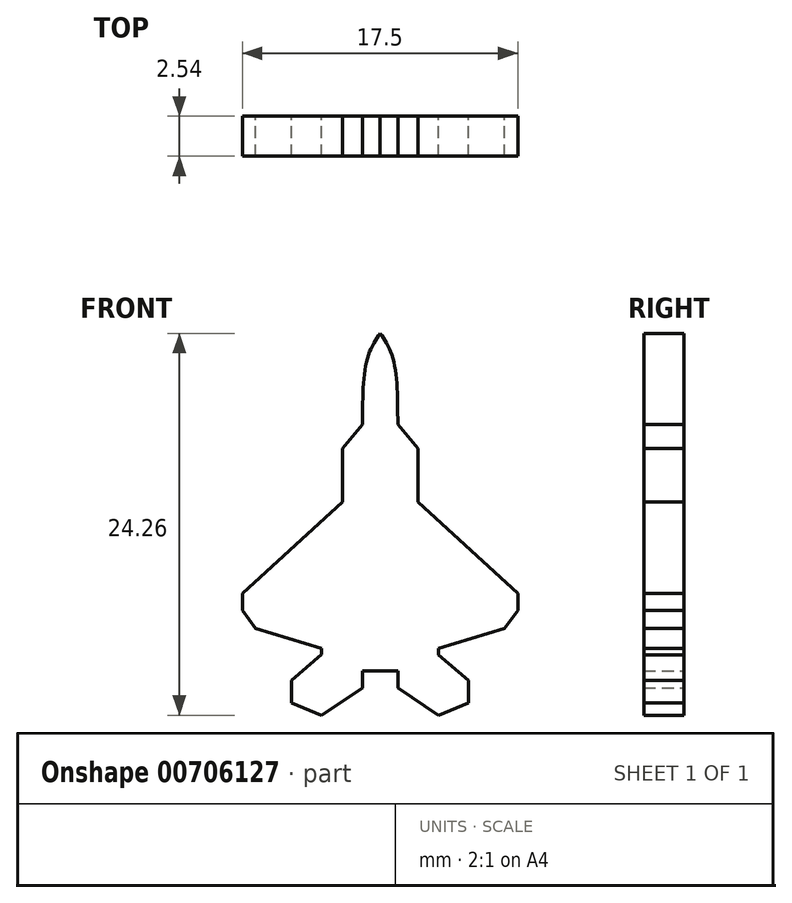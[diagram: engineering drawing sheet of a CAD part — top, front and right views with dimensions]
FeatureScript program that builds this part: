
annotation { "Feature Type Name" : "Feature", "Feature Type Description" : "" }
export const myFeature = defineFeature(function(context is Context, id is Id, definition is map)
    precondition{}
    {
        {
            var Q0;
            Q0=qCreatedBy(makeId("Front.planeOp"),FACE);
            var sketch = newSketch(context, id + "F0", { "sketchPlane" : qUnion([Q0])});
            skLineSegment(sketch, "E0.bottom", {"start": v(12.7, 12.7) * mm, "end": v(-12.7, 12.7) * mm});
            skLineSegment(sketch, "E0.top", {"start": v(12.7, -12.7) * mm, "end": v(-12.7, -12.7) * mm});
            skLineSegment(sketch, "E0.left", {"start": v(12.7, 12.7) * mm, "end": v(12.7, -12.7) * mm});
            skLineSegment(sketch, "E0.right", {"start": v(-12.7, 12.7) * mm, "end": v(-12.7, -12.7) * mm});
            skPoint(sketch, "E0.middle", {"position": v(0, 0) * mm});
            skSolve(sketch);
        }
        {
            var Q0;
            Q0 = qSketchRegion(id + "F0", true);
            extrude(context, id + "F1", {"entities" : qUnion([Q0]), "depth" : 6.35 * mm, "offsetDistance" : 25.4 * mm});
        }
        {
            var Q0;
            Q0=makeQuery(id+"F1.opExtrude","CAP_FACE",FACE,{"disambiguationData":[OSD([sQuery(id+"F0.wireOp",EDGE,"E0.bottom"),sQuery(id+"F0.wireOp",EDGE,"E0.top"),sQuery(id+"F0.wireOp",EDGE,"E0.left"),sQuery(id+"F0.wireOp",EDGE,"E0.right")])],"isStart":false});
            var sketch = newSketch(context, id + "F2", { "sketchPlane" : qUnion([Q0])});
            skLineSegment(sketch, "E1", {"start": v(-1.12, 6.26) * mm, "end": v(-2.4, 4.72) * mm});
            skLineSegment(sketch, "E2", {"start": v(-2.4, 1.33) * mm, "end": v(-8.75, -4.5) * mm});
            skLineSegment(sketch, "E3", {"start": v(-8.75, -4.5) * mm, "end": v(-8.75, -5.56) * mm});
            skLineSegment(sketch, "E4", {"start": v(-8.75, -5.56) * mm, "end": v(-7.9, -6.72) * mm});
            skLineSegment(sketch, "E5", {"start": v(-7.9, -6.72) * mm, "end": v(-3.72, -8) * mm});
            skLineSegment(sketch, "E6", {"start": v(-3.72, -8) * mm, "end": v(-5.62, -10) * mm});
            skLineSegment(sketch, "E7", {"start": v(-5.62, -10) * mm, "end": v(-5.62, -11.44) * mm});
            skLineSegment(sketch, "E8", {"start": v(-5.62, -11.44) * mm, "end": v(-3.72, -12.23) * mm});
            skLineSegment(sketch, "E9", {"start": v(-3.72, -12.23) * mm, "end": v(-1.12, -10.48) * mm});
            skLineSegment(sketch, "E10", {"start": v(-1.12, -10.48) * mm, "end": v(-1.12, -9.42) * mm});
            skLineSegment(sketch, "E11.MirrorCS", {"start": v(8.75, -4.5) * mm, "end": v(8.75, -5.56) * mm});
            skLineSegment(sketch, "E12.MirrorCS", {"start": v(8.75, -5.56) * mm, "end": v(7.9, -6.72) * mm});
            skLineSegment(sketch, "E13.MirrorCS", {"start": v(1.12, -10.48) * mm, "end": v(1.12, -9.42) * mm});
            skLineSegment(sketch, "E14.MirrorCS", {"start": v(3.72, -12.23) * mm, "end": v(1.12, -10.48) * mm});
            skLineSegment(sketch, "E15.MirrorCS", {"start": v(5.62, -11.44) * mm, "end": v(3.72, -12.23) * mm});
            skLineSegment(sketch, "E16.MirrorCS", {"start": v(1.12, 6.26) * mm, "end": v(2.4, 4.72) * mm});
            skLineSegment(sketch, "E17.MirrorCS", {"start": v(5.62, -10) * mm, "end": v(5.62, -11.44) * mm});
            skLineSegment(sketch, "E18.MirrorCS", {"start": v(2.4, 1.33) * mm, "end": v(8.75, -4.5) * mm});
            skLineSegment(sketch, "E19.MirrorCS", {"start": v(3.72, -8) * mm, "end": v(5.62, -10) * mm});
            skLineSegment(sketch, "E20.MirrorCS", {"start": v(7.9, -6.72) * mm, "end": v(3.72, -8) * mm});
            skLineSegment(sketch, "E21", {"start": v(-1.12, -9.42) * mm, "end": v(1.12, -9.42) * mm});
            skLineSegment(sketch, "E22", {"start": v(-2.4, 4.72) * mm, "end": v(-2.4, 1.33) * mm});
            skLineSegment(sketch, "E23", {"start": v(2.4, 4.72) * mm, "end": v(2.4, 1.33) * mm});
            skFitSpline(sketch, "E24", {"points": [v(0, 12.03) * mm, v(-0.82, 10.4) * mm, v(-1.12, 6.26) * mm], "startDerivative": vector(-2.38, -3.51) * mm, "endDerivative": vector(-0.03, -7.75) * mm});
            skFitSpline(sketch, "E25.MirrorCS", {"points": [v(0, 12.03) * mm, v(0.82, 10.4) * mm, v(1.12, 6.26) * mm], "startDerivative": vector(2.38, -3.51) * mm, "endDerivative": vector(0.03, -7.75) * mm});
            skSolve(sketch);
        }
        {
            var Q0;
            Q0 = qSketchRegion(id + "F2", true);
            extrude(context, id + "F3", {"entities" : qUnion([Q0]), "operationType" : NewBodyOperationType.ADD, "depth" : 2.54 * mm, "offsetDistance" : 25.4 * mm});
        }
        {
            var Q0;
            Q0=makeQuery(id+"F1.opExtrude","SWEPT_FACE",FACE,{"disambiguationData":[OSD([sQuery(id+"F0.wireOp",EDGE,"E0.left")])]});
            var sketch = newSketch(context, id + "F4", { "sketchPlane" : qUnion([Q0])});
            skLineSegment(sketch, "E26.bottom", {"start": v(-6.35, 12.7) * mm, "end": v(0, 12.7) * mm});
            skLineSegment(sketch, "E26.top", {"start": v(-6.35, -12.7) * mm, "end": v(0, -12.7) * mm});
            skLineSegment(sketch, "E26.left", {"start": v(-6.35, 12.7) * mm, "end": v(-6.35, -12.7) * mm});
            skLineSegment(sketch, "E26.right", {"start": v(0, 12.7) * mm, "end": v(0, -12.7) * mm});
            skSolve(sketch);
        }
        {
            var Q0;
            Q0 = qSketchRegion(id + "F4", true);
            extrude(context, id + "F5", {"entities" : qUnion([Q0]), "operationType" : NewBodyOperationType.REMOVE, "endBound" : BoundingType.THROUGH_ALL, "oppositeDirection" : true, "depth" : 25.4 * mm, "offsetDistance" : 25.4 * mm});
        }
        {
            var Q0;
            Q0=makeQuery(id+"F3.opExtrude","CAP_FACE",FACE,{"disambiguationData":[OSD([sQuery(id+"F2.wireOp",EDGE,"E1"),sQuery(id+"F2.wireOp",EDGE,"E2"),sQuery(id+"F2.wireOp",EDGE,"E3"),sQuery(id+"F2.wireOp",EDGE,"E4"),sQuery(id+"F2.wireOp",EDGE,"E5"),sQuery(id+"F2.wireOp",EDGE,"E6"),sQuery(id+"F2.wireOp",EDGE,"E7"),sQuery(id+"F2.wireOp",EDGE,"E8"),sQuery(id+"F2.wireOp",EDGE,"E9"),sQuery(id+"F2.wireOp",EDGE,"E10"),sQuery(id+"F2.wireOp",EDGE,"E11.MirrorCS"),sQuery(id+"F2.wireOp",EDGE,"E12.MirrorCS"),sQuery(id+"F2.wireOp",EDGE,"E13.MirrorCS"),sQuery(id+"F2.wireOp",EDGE,"E14.MirrorCS"),sQuery(id+"F2.wireOp",EDGE,"E15.MirrorCS"),sQuery(id+"F2.wireOp",EDGE,"E16.MirrorCS"),sQuery(id+"F2.wireOp",EDGE,"E17.MirrorCS"),sQuery(id+"F2.wireOp",EDGE,"E18.MirrorCS"),sQuery(id+"F2.wireOp",EDGE,"E19.MirrorCS"),sQuery(id+"F2.wireOp",EDGE,"E20.MirrorCS"),sQuery(id+"F2.wireOp",EDGE,"E21"),sQuery(id+"F2.wireOp",EDGE,"E22"),sQuery(id+"F2.wireOp",EDGE,"E23"),sQuery(id+"F2.wireOp",EDGE,"E24"),sQuery(id+"F2.wireOp",EDGE,"E25.MirrorCS")])],"isStart":false});
            var sketch = newSketch(context, id + "F6", { "sketchPlane" : qUnion([Q0])});
            skLineSegment(sketch, "E27", {"start": v(-5.62, -10) * mm, "end": v(-3.72, -8.37) * mm});
            skLineSegment(sketch, "E28", {"start": v(-3.72, -8.37) * mm, "end": v(-3.72, -8) * mm});
            skSolve(sketch);
        }
        {
            var Q0;
            Q0=makeQuery(id+"F6.imprint","IMPRINT",FACE,{"disambiguationData":[TD([[makeQuery(id+"F6.imprint","IMPRINT",EDGE,{"derivedFrom":sQuery(id+"F6.wireOp",EDGE,"E27")}),1.0]])]});
            extrude(context, id + "F7", {"entities" : qUnion([Q0]), "operationType" : NewBodyOperationType.REMOVE, "endBound" : BoundingType.THROUGH_ALL, "oppositeDirection" : true, "depth" : 25.4 * mm, "offsetDistance" : 25.4 * mm});
        }
        {
            var Q0;
            Q0=makeQuery(id+"F3.opExtrude","CAP_FACE",FACE,{"disambiguationData":[OSD([sQuery(id+"F2.wireOp",EDGE,"E1"),sQuery(id+"F2.wireOp",EDGE,"E2"),sQuery(id+"F2.wireOp",EDGE,"E3"),sQuery(id+"F2.wireOp",EDGE,"E4"),sQuery(id+"F2.wireOp",EDGE,"E5"),sQuery(id+"F2.wireOp",EDGE,"E6"),sQuery(id+"F2.wireOp",EDGE,"E7"),sQuery(id+"F2.wireOp",EDGE,"E8"),sQuery(id+"F2.wireOp",EDGE,"E9"),sQuery(id+"F2.wireOp",EDGE,"E10"),sQuery(id+"F2.wireOp",EDGE,"E11.MirrorCS"),sQuery(id+"F2.wireOp",EDGE,"E12.MirrorCS"),sQuery(id+"F2.wireOp",EDGE,"E13.MirrorCS"),sQuery(id+"F2.wireOp",EDGE,"E14.MirrorCS"),sQuery(id+"F2.wireOp",EDGE,"E15.MirrorCS"),sQuery(id+"F2.wireOp",EDGE,"E16.MirrorCS"),sQuery(id+"F2.wireOp",EDGE,"E17.MirrorCS"),sQuery(id+"F2.wireOp",EDGE,"E18.MirrorCS"),sQuery(id+"F2.wireOp",EDGE,"E19.MirrorCS"),sQuery(id+"F2.wireOp",EDGE,"E20.MirrorCS"),sQuery(id+"F2.wireOp",EDGE,"E21"),sQuery(id+"F2.wireOp",EDGE,"E22"),sQuery(id+"F2.wireOp",EDGE,"E23"),sQuery(id+"F2.wireOp",EDGE,"E24"),sQuery(id+"F2.wireOp",EDGE,"E25.MirrorCS")])],"isStart":false});
            var sketch = newSketch(context, id + "F8", { "sketchPlane" : qUnion([Q0])});
            skLineSegment(sketch, "E29", {"start": v(5.62, -10) * mm, "end": v(3.72, -8.4) * mm});
            skLineSegment(sketch, "E30", {"start": v(3.72, -8.4) * mm, "end": v(3.72, -8) * mm});
            skSolve(sketch);
        }
        {
            var Q0;
            Q0=makeQuery(id+"F8.imprint","IMPRINT",FACE,{"disambiguationData":[TD([[makeQuery(id+"F8.imprint","IMPRINT",EDGE,{"derivedFrom":sQuery(id+"F8.wireOp",EDGE,"E29")}),-1.0]])]});
            extrude(context, id + "F9", {"entities" : qUnion([Q0]), "operationType" : NewBodyOperationType.REMOVE, "endBound" : BoundingType.THROUGH_ALL, "oppositeDirection" : true, "depth" : 25.4 * mm, "offsetDistance" : 25.4 * mm});
        }
    });
